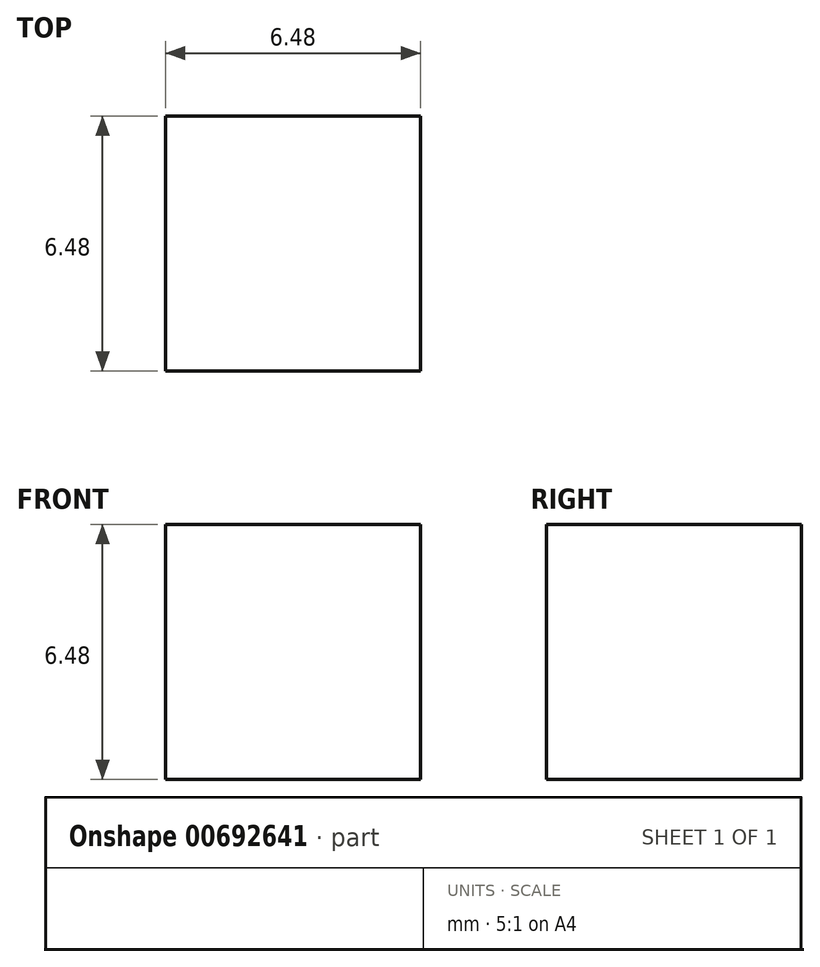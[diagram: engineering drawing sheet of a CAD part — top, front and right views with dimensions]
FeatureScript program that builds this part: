
annotation { "Feature Type Name" : "Feature", "Feature Type Description" : "" }
export const myFeature = defineFeature(function(context is Context, id is Id, definition is map)
    precondition{}
    {
        {
            var Q0;
            Q0=qCreatedBy(makeId("Top.planeOp"),FACE);
            var sketch = newSketch(context, id + "F0", { "sketchPlane" : qUnion([Q0])});
            skLineSegment(sketch, "E0.bottom", {"start": v(-13.08, 14.86) * mm, "end": v(-6.6, 14.86) * mm});
            skLineSegment(sketch, "E0.top", {"start": v(-13.08, 8.38) * mm, "end": v(-6.6, 8.38) * mm});
            skLineSegment(sketch, "E0.left", {"start": v(-13.08, 14.86) * mm, "end": v(-13.08, 8.38) * mm});
            skLineSegment(sketch, "E0.right", {"start": v(-6.6, 14.86) * mm, "end": v(-6.6, 8.38) * mm});
            skSolve(sketch);
        }
        {
            var Q0;
            Q0=makeQuery(id+"F0.imprint","IMPRINT",FACE,{"disambiguationData":[TD([[makeQuery(id+"F0.imprint","IMPRINT",EDGE,{"derivedFrom":sQuery(id+"F0.wireOp",EDGE,"E0.bottom")}),-1.0]])]});
            extrude(context, id + "F1", {"entities" : qUnion([Q0]), "depth" : 6.48 * mm, "offsetDistance" : 25.4 * mm});
        }
    });
